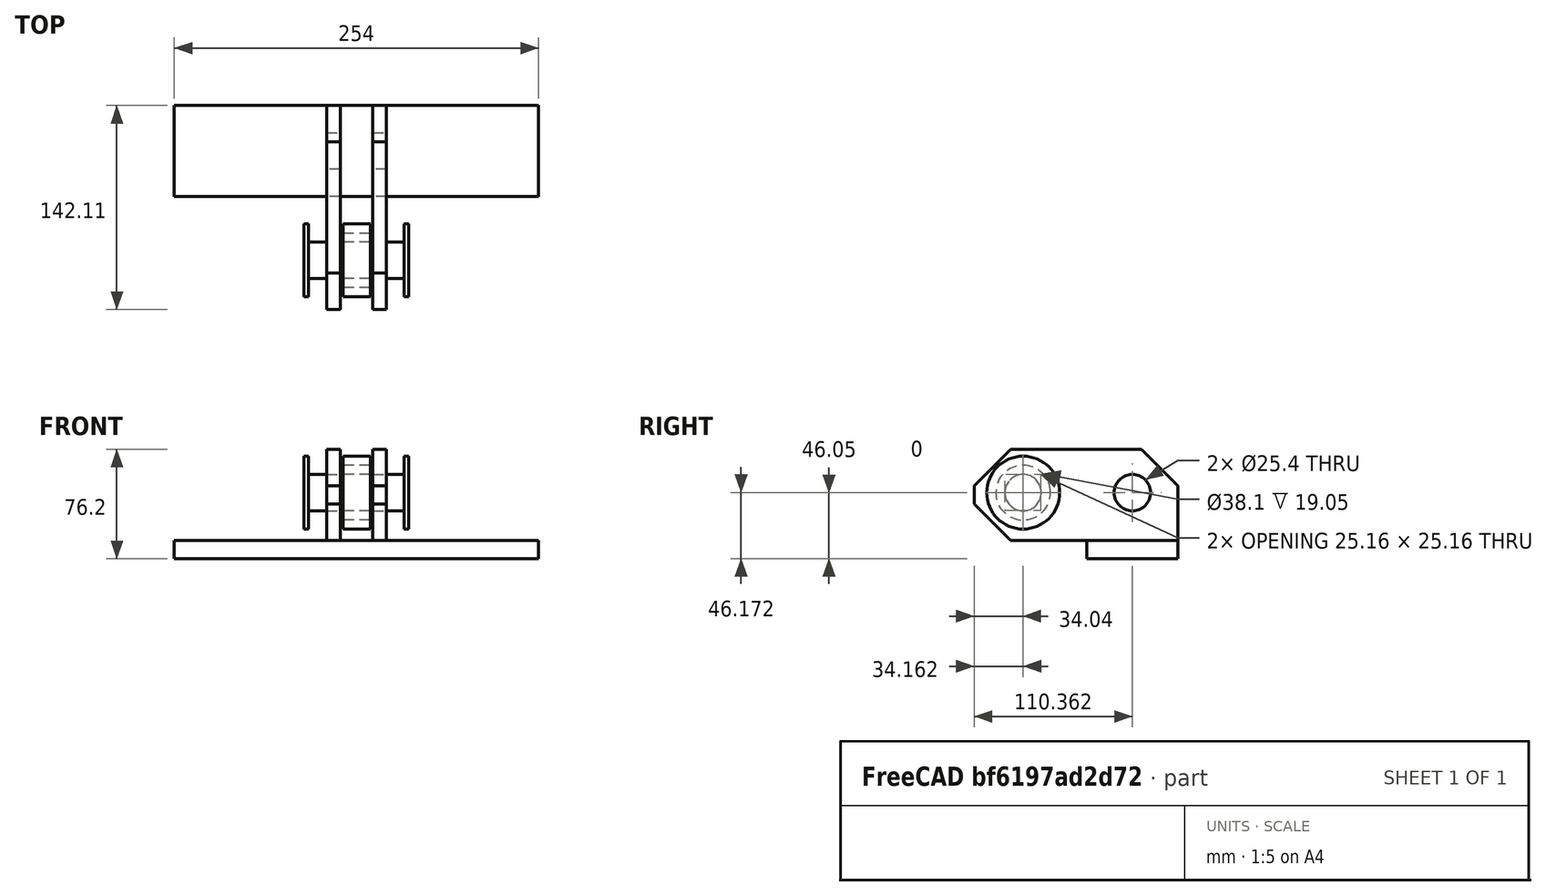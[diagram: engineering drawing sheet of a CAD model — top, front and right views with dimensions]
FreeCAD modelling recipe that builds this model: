
FCSTD DOCUMENT  (FreeCAD 0.16R6702 (Git))
Label: trackunitinnerfused
License: All rights reserved
LicenseURL: http://en.wikipedia.org/wiki/All_rights_reserved
objects: App::FeaturePython×6, Part::FeaturePython×5, Part::Part2DObjectPython×1, App::DocumentObjectGroup×1, Part::MultiFuse×1
note: 7 computed .brp shape members not serialized (recipe doc carries the construction recipe); baked Part::Feature solids carry a one-line shape summary decoded from their .brp

FEATURE [Part::FeaturePython] trackpadbasic_01  # a2plus imported part (geometry in sourceFile) (typed FeaturePython)
  fixedPosition = true
  sourceFile = <userpath>/Documents/Open Source Ecology/Bulldozer/Tracks FreeCAD Files/trackpadbasic.FCStd
  timeLastImport = 1463488866
  updateColors = true
FEATURE [Part::FeaturePython] TrackChainLink_01  # a2plus imported part (geometry in sourceFile) (typed FeaturePython)
  Placement = pos=(20.8661,-24.8857,18.54) rot=(0.57735,-0.57735,-0.57735;2.0944rad)
  fixedPosition = false
  sourceFile = <userpath>/Documents/Open Source Ecology/Bulldozer/Tracks FreeCAD Files/TrackChainLink.FCStd
  timeLastImport = 1463487855
  updateColors = true
FEATURE [Part::Part2DObjectPython] Circle  # Draft 2D object (typed FeaturePython)
  FirstAngle = 0
  LastAngle = 0
  MakeFace = true
  Placement = pos=(0,60.6716,12.7) rot=(1,0,0;1.5708rad)
  Radius = 20.8661
FEATURE [App::DocumentObjectGroup] Construction
  Group = -> [Circle]
FEATURE [Part::FeaturePython] TrackChainLink_002  # a2plus imported part (geometry in sourceFile) (typed FeaturePython)
  Placement = pos=(-11.3411,-24.8857,18.54) rot=(0.57735,-0.57735,-0.57735;2.0944rad)
  fixedPosition = false
  sourceFile = <userpath>/Documents/Open Source Ecology/Bulldozer/Tracks FreeCAD Files/TrackChainLink.FCStd
  timeLastImport = 1463487855
  updateColors = true
FEATURE [Part::FeaturePython] trackroller_01  # a2plus imported part (geometry in sourceFile) (typed FeaturePython)
  Placement = pos=(-9.43522,-47.2784,46.0502) rot=(0.57735,0.57735,0.57735;2.0944rad)
  fixedPosition = false
  sourceFile = <userpath>/Documents/Open Source Ecology/Bulldozer/Tracks FreeCAD Files/trackroller.FCStd
  timeLastImport = 1463678662
  updateColors = true
FEATURE [App::FeaturePython] axialConstraint01  # a2plus constraint (typed FeaturePython)
  Object1 = TrackChainLink_01
  Object2 = trackroller_01
  SubElement1 = Face9
  SubElement2 = Face2
  Type = axial
  directionConstraint = 1
  lockRotation = false
FEATURE [App::FeaturePython] axialConstraint01_mirror  label="axialConstraint01_"  # a2plus constraint (typed FeaturePython)
  Object1 = TrackChainLink_01
  Object2 = trackroller_01
  SubElement1 = Face9
  SubElement2 = Face2
  Type = axial
  directionConstraint = 1
  lockRotation = false
FEATURE [Part::FeaturePython] trackpin_002  # a2plus imported part (geometry in sourceFile) (typed FeaturePython)
  Placement = pos=(36.3186,-47.2784,46.0502) rot=(0,-1,0;1.5708rad)
  fixedPosition = false
  sourceFile = <userpath>/Documents/Open Source Ecology/Bulldozer/Tracks FreeCAD Files/trackpin.FCStd
  timeLastImport = 1463834196
  updateColors = true
FEATURE [App::FeaturePython] axialConstraint03  # a2plus constraint (typed FeaturePython)
  Object1 = trackroller_01
  Object2 = TrackChainLink_002
  SubElement1 = Face1
  SubElement2 = Face9
  Type = axial
  directionConstraint = 1
  lockRotation = false
FEATURE [App::FeaturePython] axialConstraint03_mirror  label="axialConstraint03_"  # a2plus constraint (typed FeaturePython)
  Object1 = trackroller_01
  Object2 = TrackChainLink_002
  SubElement1 = Face1
  SubElement2 = Face9
  Type = axial
  directionConstraint = 1
  lockRotation = false
FEATURE [App::FeaturePython] axialConstraint02  # a2plus constraint (typed FeaturePython)
  Object1 = TrackChainLink_01
  Object2 = trackpin_002
  SubElement1 = Face9
  SubElement2 = Face4
  Type = axial
  directionConstraint = 1
  lockRotation = false
FEATURE [App::FeaturePython] axialConstraint02_mirror  label="axialConstraint02_"  # a2plus constraint (typed FeaturePython)
  Object1 = TrackChainLink_01
  Object2 = trackpin_002
  SubElement1 = Face9
  SubElement2 = Face4
  Type = axial
  directionConstraint = 1
  lockRotation = false
FEATURE [Part::MultiFuse] Fusion
  Shapes = -> [trackpadbasic_01,TrackChainLink_01,TrackChainLink_002,trackroller_01,trackpin_002]
